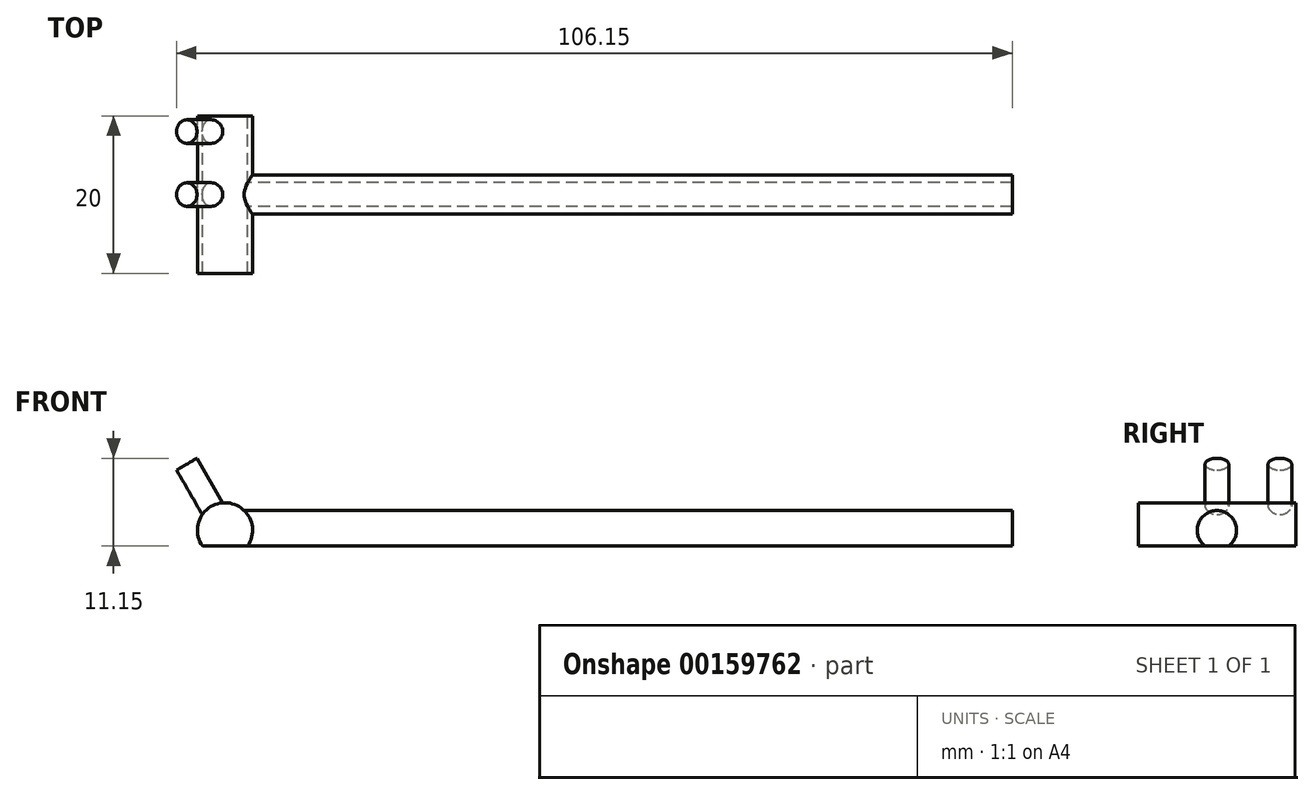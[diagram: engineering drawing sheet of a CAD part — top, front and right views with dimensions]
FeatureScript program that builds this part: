
annotation { "Feature Type Name" : "Feature", "Feature Type Description" : "" }
export const myFeature = defineFeature(function(context is Context, id is Id, definition is map)
    precondition{}
    {
        {
            var Q0;
            Q0=qCreatedBy(makeId("Front.planeOp"),FACE);
            var sketch = newSketch(context, id + "F0", { "sketchPlane" : qUnion([Q0])});
            skArc(sketch, "E0", {"start": v(2.87, -2) * mm, "mid": v(0, 3.5) * mm, "end": v(-2.87, -2) * mm});
            skLineSegment(sketch, "E1", {"start": v(-2.87, -2) * mm, "end": v(2.87, -2) * mm});
            skSolve(sketch);
        }
        {
            var Q0;
            Q0=makeQuery(id+"F0.imprint","IMPRINT",FACE,{"disambiguationData":[TD([[makeQuery(id+"F0.imprint","IMPRINT",EDGE,{"derivedFrom":sQuery(id+"F0.wireOp",EDGE,"E0")}),1.0]])]});
            extrude(context, id + "F1", {"entities" : qUnion([Q0]), "endBound" : BoundingType.SYMMETRIC, "depth" : 20 * mm});
        }
        {
            var Q0;
            Q0=qCreatedBy(makeId("Right.planeOp"),FACE);
            var sketch = newSketch(context, id + "F2", { "sketchPlane" : qUnion([Q0])});
            skArc(sketch, "E2", {"start": v(1.5, -2) * mm, "mid": v(0, 2.5) * mm, "end": v(-1.5, -2) * mm});
            skLineSegment(sketch, "E3.0", {"start": v(-1.5, -2) * mm, "end": v(1.5, -2) * mm});
            skPoint(sketch, "E4.orphan", {"position": v(10, -2) * mm});
            skPoint(sketch, "E5.orphan", {"position": v(-10, -2) * mm});
            skSolve(sketch);
        }
        {
            var Q0;
            Q0 = qSketchRegion(id + "F2", true);
            extrude(context, id + "F3", {"entities" : qUnion([Q0]), "operationType" : NewBodyOperationType.ADD, "depth" : 100 * mm});
        }
        {
            var Q0;
            Q0=qCreatedBy(makeId("Top.planeOp"),FACE);
            var Q1;
            {var subQ0=sQuery(id+"F0.wireOp",EDGE,"E1");var subQ1=sQuery(id+"F0.wireOp",EDGE,"E0");Q1=makeQuery(id+"F1.opExtrude","SWEPT_EDGE",EDGE,{"disambiguationData":[OSD([subQ1,subQ0]),TDD([makeQuery(id+"F0.imprint","INTERSECT",VERTEX,{"disambiguationData":[OD(1.0)],"derivedFrom":[subQ1,subQ0]})])]});}
            cPlane(context, id + "F4", {"entities" : qUnion([Q0, Q1]), "cplaneType" : CPlaneType.LINE_ANGLE, "offset" : 25 * mm, "angle" : 330 * degree, "width" : 150 * mm, "height" : 150 * mm});
        }
        {
            var Q0;
            Q0=qCreatedBy(id+"F4.planeOp",FACE);
            var sketch = newSketch(context, id + "F5", { "sketchPlane" : qUnion([Q0])});
            skCircle(sketch, "E6", {"center": v(0, 0) * mm, "radius": 1.5 * mm});
            skCircle(sketch, "E7.0.1.0", {"center": v(0, -8) * mm, "radius": 1.5 * mm});
            skLineSegment(sketch, "E7.direction1", {"start": v(0, 0) * mm, "end": v(-25, 0) * mm, "construction": true});
            skLineSegment(sketch, "E7.direction2", {"start": v(0, 0) * mm, "end": v(0, -8) * mm, "construction": true});
            skSolve(sketch);
        }
        {
            var Q0;
            Q0 = qSketchRegion(id + "F5", true);
            extrude(context, id + "F6", {"entities" : qUnion([Q0]), "operationType" : NewBodyOperationType.ADD, "oppositeDirection" : true, "depth" : 10 * mm});
        }
    });
